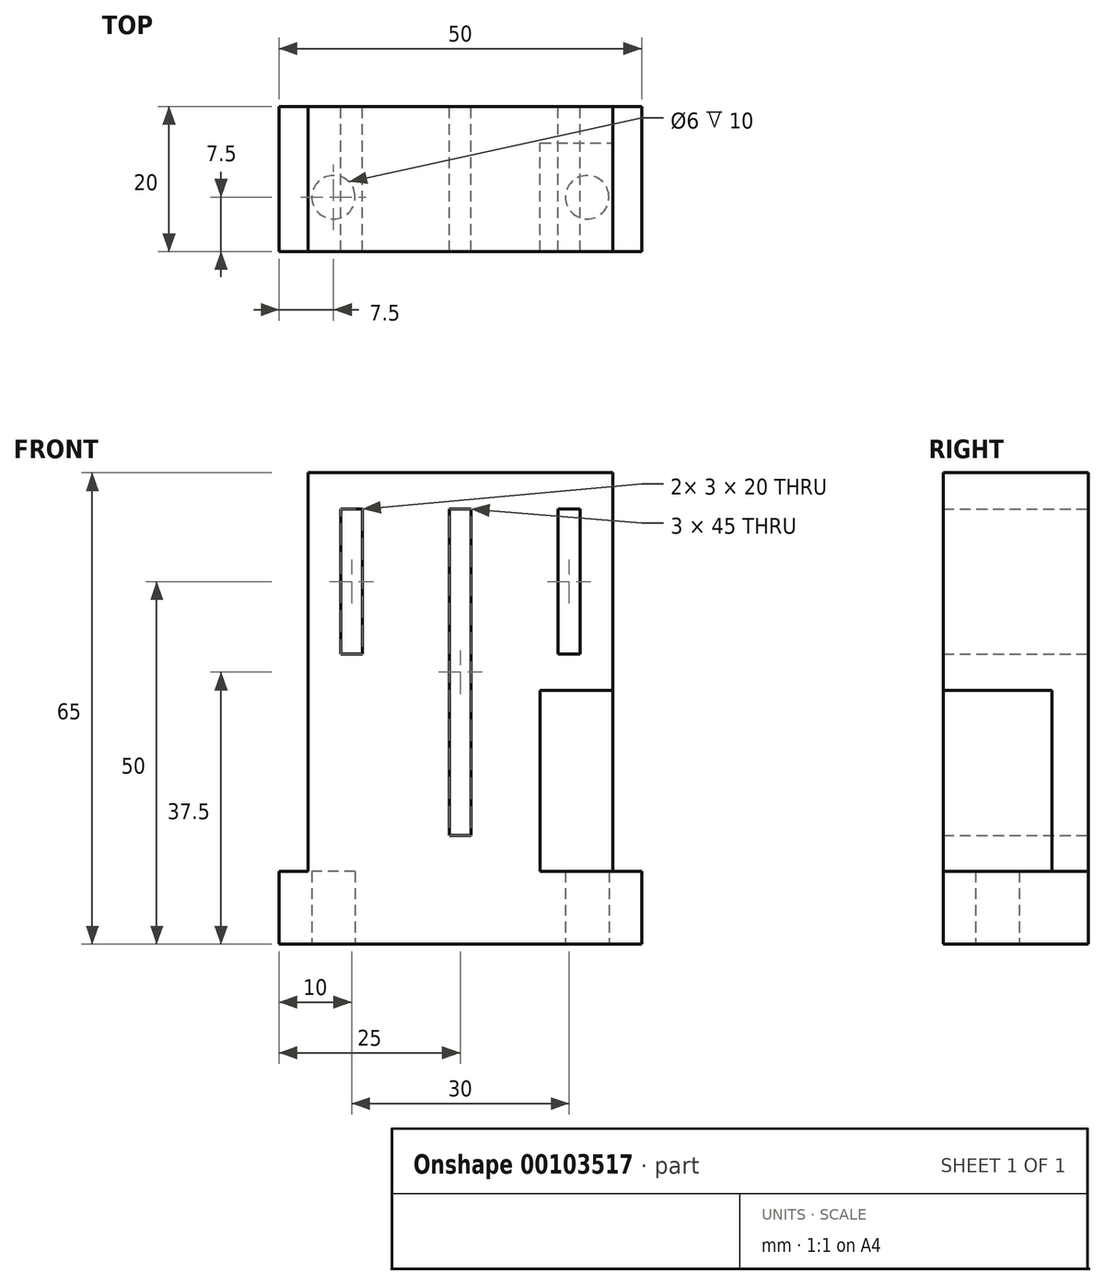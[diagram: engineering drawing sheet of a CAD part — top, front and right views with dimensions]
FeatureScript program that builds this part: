
annotation { "Feature Type Name" : "Feature", "Feature Type Description" : "" }
export const myFeature = defineFeature(function(context is Context, id is Id, definition is map)
    precondition{}
    {
        {
            var Q0;
            Q0=qCreatedBy(makeId("Top.planeOp"),FACE);
            var sketch = newSketch(context, id + "F0", { "sketchPlane" : qUnion([Q0])});
            skLineSegment(sketch, "E0.bottom", {"start": v(25, 7.5) * mm, "end": v(-25, 7.5) * mm});
            skLineSegment(sketch, "E0.top", {"start": v(25, -12.5) * mm, "end": v(-25, -12.5) * mm});
            skLineSegment(sketch, "E0.left", {"start": v(25, 7.5) * mm, "end": v(25, -12.5) * mm});
            skLineSegment(sketch, "E0.right", {"start": v(-25, 7.5) * mm, "end": v(-25, -12.5) * mm});
            skPoint(sketch, "E0.middle", {"position": v(0, 0) * mm});
            skCircle(sketch, "E1", {"center": v(-17.5, -5) * mm, "radius": 3 * mm});
            skCircle(sketch, "E2.MirrorC", {"center": v(17.5, -5) * mm, "radius": 3 * mm});
            skSolve(sketch);
        }
        {
            var Q0;
            Q0=makeQuery(id+"F0.imprint","IMPRINT",FACE,{"disambiguationData":[TD([[makeQuery(id+"F0.imprint","IMPRINT",EDGE,{"derivedFrom":sQuery(id+"F0.wireOp",EDGE,"E0.bottom")}),1.0]])]});
            extrude(context, id + "F1", {"entities" : qUnion([Q0]), "depth" : 10 * mm});
        }
        {
            var Q0;
            Q0=makeQuery(id+"F1.opExtrude","SWEPT_FACE",FACE,{"disambiguationData":[OSD([sQuery(id+"F0.wireOp",EDGE,"E0.bottom")])]});
            var sketch = newSketch(context, id + "F2", { "sketchPlane" : qUnion([Q0])});
            skLineSegment(sketch, "E3.bottom", {"start": v(-21, 10) * mm, "end": v(21, 10) * mm});
            skLineSegment(sketch, "E3.top", {"start": v(-21, 65) * mm, "end": v(21, 65) * mm});
            skLineSegment(sketch, "E3.left", {"start": v(-21, 10) * mm, "end": v(-21, 65) * mm});
            skLineSegment(sketch, "E3.right", {"start": v(21, 10) * mm, "end": v(21, 65) * mm});
            skSolve(sketch);
        }
        {
            var Q0;
            {var subQ0=sQuery(id+"F2.wireOp",EDGE,"E3.top");Q0=makeQuery(id+"F2.imprint","IMPRINT",FACE,{"disambiguationData":[TD([[makeQuery(id+"F2.imprint","IMPRINT",EDGE,{"derivedFrom":subQ0}),-1.0]])]});}
            extrude(context, id + "F3", {"entities" : qUnion([Q0]), "operationType" : NewBodyOperationType.ADD, "oppositeDirection" : true, "offsetDistance" : 25 * mm, "depth" : 20 * mm});
        }
        {
            var Q0;
            {var subQ0=sQuery(id+"F0.wireOp",EDGE,"E0.bottom");Q0=makeQuery(id+"F3.boolean.opBoolean","MERGE",FACE,{"derivedFrom":[makeQuery(id+"F1.opExtrude","SWEPT_FACE",FACE,{"disambiguationData":[OSD([subQ0])]}),makeQuery(id+"F3.opExtrude","CAP_FACE",FACE,{"disambiguationData":[OSD([subQ0,sQuery(id+"F2.wireOp",EDGE,"E3.top"),sQuery(id+"F2.wireOp",EDGE,"E3.left"),sQuery(id+"F2.wireOp",EDGE,"E3.right")])],"isStart":true})]});}
            var sketch = newSketch(context, id + "F4", { "sketchPlane" : qUnion([Q0])});
            skLineSegment(sketch, "E4.bottom", {"start": v(-16.5, 60) * mm, "end": v(-13.5, 60) * mm});
            skLineSegment(sketch, "E4.top", {"start": v(-16.5, 40) * mm, "end": v(-13.5, 40) * mm});
            skLineSegment(sketch, "E4.left", {"start": v(-16.5, 60) * mm, "end": v(-16.5, 40) * mm});
            skLineSegment(sketch, "E4.right", {"start": v(-13.5, 60) * mm, "end": v(-13.5, 40) * mm});
            skLineSegment(sketch, "E5.bottom", {"start": v(-1.5, 60) * mm, "end": v(1.5, 60) * mm});
            skLineSegment(sketch, "E5.top", {"start": v(-1.5, 15) * mm, "end": v(1.5, 15) * mm});
            skLineSegment(sketch, "E5.left", {"start": v(1.5, 60) * mm, "end": v(1.5, 15) * mm});
            skLineSegment(sketch, "E5.right", {"start": v(-1.5, 60) * mm, "end": v(-1.5, 15) * mm});
            skLineSegment(sketch, "E6.bottom", {"start": v(13.5, 60) * mm, "end": v(16.5, 60) * mm});
            skLineSegment(sketch, "E6.top", {"start": v(13.5, 40) * mm, "end": v(16.5, 40) * mm});
            skLineSegment(sketch, "E6.left", {"start": v(13.5, 60) * mm, "end": v(13.5, 40) * mm});
            skLineSegment(sketch, "E6.right", {"start": v(16.5, 60) * mm, "end": v(16.5, 40) * mm});
            skSolve(sketch);
        }
        {
            var Q0;
            Q0=makeQuery(id+"F4.imprint","IMPRINT",FACE,{"disambiguationData":[TD([[makeQuery(id+"F4.imprint","IMPRINT",EDGE,{"derivedFrom":sQuery(id+"F4.wireOp",EDGE,"E4.bottom")}),-1.0]])]});
            var Q1;
            Q1=makeQuery(id+"F4.imprint","IMPRINT",FACE,{"disambiguationData":[TD([[makeQuery(id+"F4.imprint","IMPRINT",EDGE,{"derivedFrom":sQuery(id+"F4.wireOp",EDGE,"E5.bottom")}),-1.0]])]});
            var Q2;
            Q2=makeQuery(id+"F4.imprint","IMPRINT",FACE,{"disambiguationData":[TD([[makeQuery(id+"F4.imprint","IMPRINT",EDGE,{"derivedFrom":sQuery(id+"F4.wireOp",EDGE,"E6.bottom")}),-1.0]])]});
            extrude(context, id + "F5", {"entities" : qUnion([Q0, Q1, Q2]), "operationType" : NewBodyOperationType.REMOVE, "endBound" : BoundingType.UP_TO_NEXT, "oppositeDirection" : true, "depth" : 25 * mm, "offsetDistance" : 25 * mm});
        }
        {
            var Q0;
            Q0=makeQuery(id+"F3.opExtrude","SWEPT_FACE",FACE,{"disambiguationData":[OSD([sQuery(id+"F2.wireOp",EDGE,"E3.left")])]});
            var sketch = newSketch(context, id + "F6", { "sketchPlane" : qUnion([Q0])});
            skLineSegment(sketch, "E7.bottom", {"start": v(-12.5, 10) * mm, "end": v(2.5, 10) * mm});
            skLineSegment(sketch, "E7.top", {"start": v(-12.5, 35) * mm, "end": v(2.5, 35) * mm});
            skLineSegment(sketch, "E7.left", {"start": v(-12.5, 10) * mm, "end": v(-12.5, 35) * mm});
            skLineSegment(sketch, "E7.right", {"start": v(2.5, 10) * mm, "end": v(2.5, 35) * mm});
            skSolve(sketch);
        }
        {
            var Q0;
            Q0=makeQuery(id+"F6.imprint","IMPRINT",FACE,{"disambiguationData":[TD([[makeQuery(id+"F6.imprint","IMPRINT",EDGE,{"derivedFrom":sQuery(id+"F6.wireOp",EDGE,"E7.bottom")}),1.0]])]});
            extrude(context, id + "F7", {"entities" : qUnion([Q0]), "operationType" : NewBodyOperationType.REMOVE, "oppositeDirection" : true, "depth" : 10 * mm, "offsetDistance" : 25 * mm});
        }
    });
